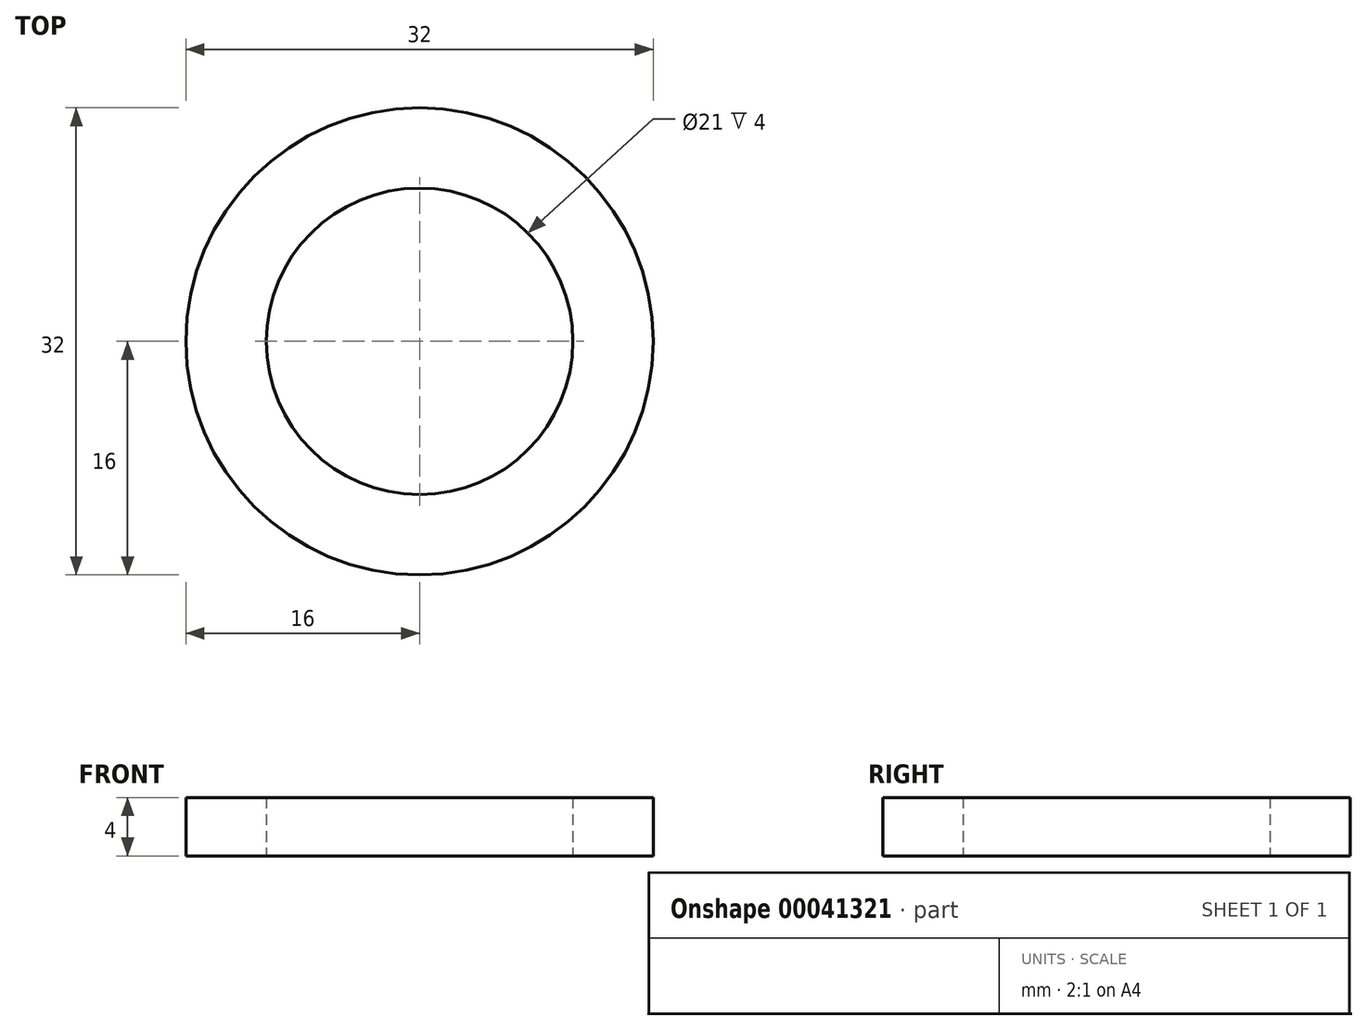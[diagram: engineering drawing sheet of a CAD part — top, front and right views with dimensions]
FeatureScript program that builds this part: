
annotation { "Feature Type Name" : "Feature", "Feature Type Description" : "" }
export const myFeature = defineFeature(function(context is Context, id is Id, definition is map)
    precondition{}
    {
        {
            var Q0;
            Q0=qCreatedBy(makeId("Top.planeOp"),FACE);
            var sketch = newSketch(context, id + "F0", { "sketchPlane" : qUnion([Q0])});
            skCircle(sketch, "E0", {"center": v(0, -0.29) * mm, "radius": 16 * mm});
            skCircle(sketch, "E1", {"center": v(0, -0.29) * mm, "radius": 10.5 * mm});
            skSolve(sketch);
        }
        {
            var Q0;
            Q0=makeQuery(id+"F0.imprint","IMPRINT",FACE,{"disambiguationData":[TD([[makeQuery(id+"F0.imprint","IMPRINT",EDGE,{"derivedFrom":sQuery(id+"F0.wireOp",EDGE,"E0")}),1.0]])]});
            extrude(context, id + "F1", {"entities" : qUnion([Q0]), "depth" : 4 * mm});
        }
    });
